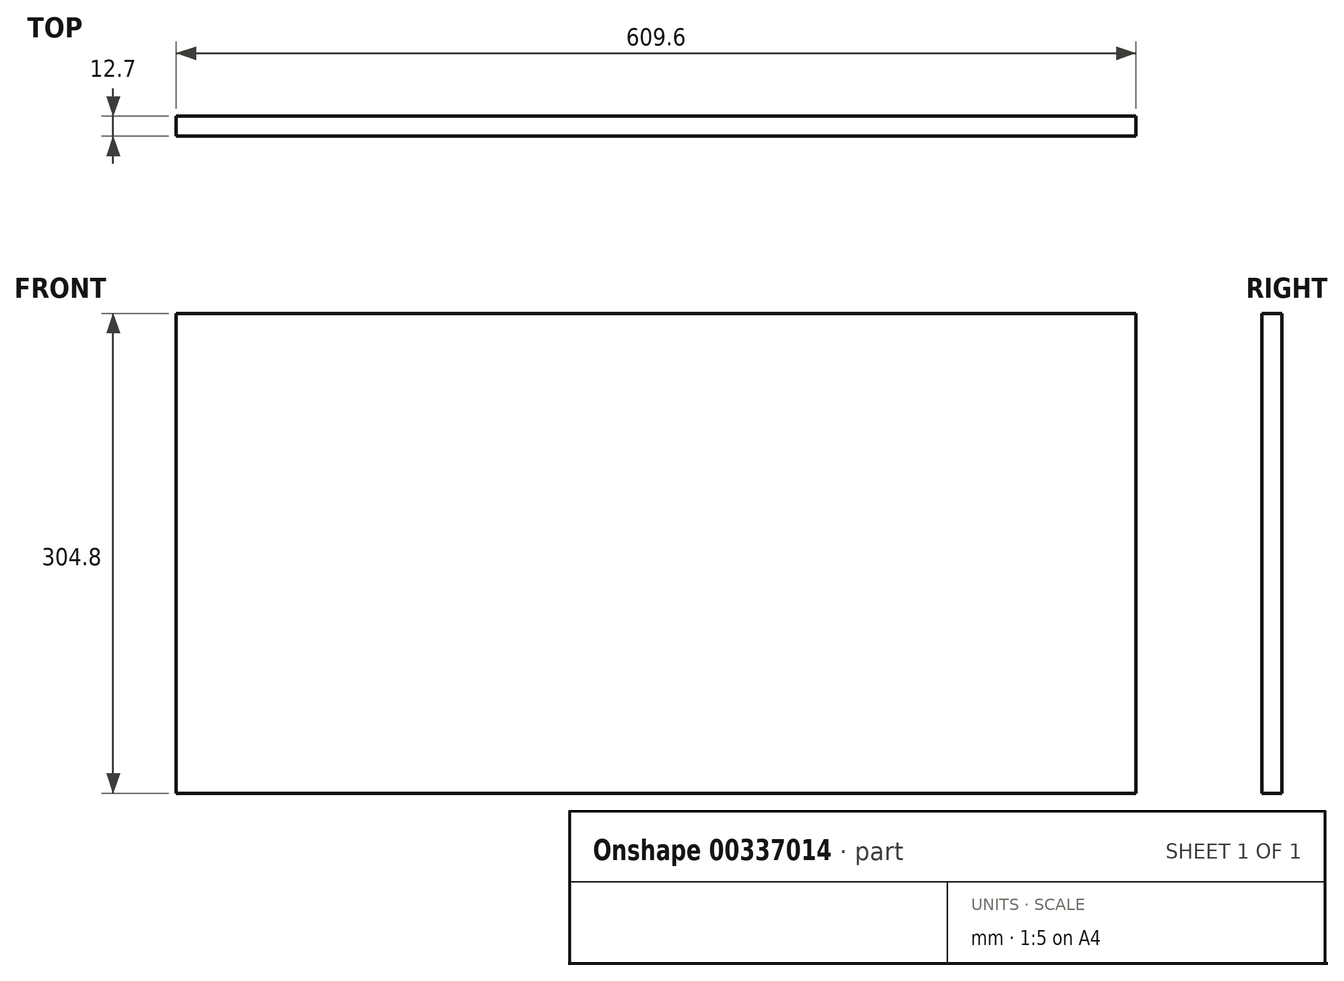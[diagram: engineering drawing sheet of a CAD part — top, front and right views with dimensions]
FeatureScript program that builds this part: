
annotation { "Feature Type Name" : "Feature", "Feature Type Description" : "" }
export const myFeature = defineFeature(function(context is Context, id is Id, definition is map)
    precondition{}
    {
        {
            var Q0;
            Q0=qCreatedBy(makeId("Front.planeOp"),FACE);
            var sketch = newSketch(context, id + "F0", { "sketchPlane" : qUnion([Q0])});
            skLineSegment(sketch, "E0.bottom", {"start": v(-304.58, 27.5) * mm, "end": v(305.02, 27.5) * mm});
            skLineSegment(sketch, "E0.top", {"start": v(-304.58, -277.3) * mm, "end": v(305.02, -277.3) * mm});
            skLineSegment(sketch, "E0.left", {"start": v(-304.58, 27.5) * mm, "end": v(-304.58, -277.3) * mm});
            skLineSegment(sketch, "E0.right", {"start": v(305.02, 27.5) * mm, "end": v(305.02, -277.3) * mm});
            skSolve(sketch);
        }
        {
            var Q0;
            Q0=makeQuery(id+"F0.imprint","IMPRINT",FACE,{"disambiguationData":[TD([[makeQuery(id+"F0.imprint","IMPRINT",EDGE,{"derivedFrom":sQuery(id+"F0.wireOp",EDGE,"E0.bottom")}),-1.0]])]});
            extrude(context, id + "F1", {"entities" : qUnion([Q0]), "depth" : 12.7 * mm});
        }
    });
